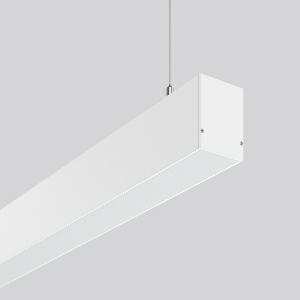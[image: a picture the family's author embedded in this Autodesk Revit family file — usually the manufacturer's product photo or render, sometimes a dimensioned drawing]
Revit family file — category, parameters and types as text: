
# Revit family: less_is_more_50_312320_002_a674
name_source: partatom
category: Lighting Fixtures
units: mm (PartAtom-declared; Revit-internal decimal feet)

## family parameters
Cut with Voids When Loaded = No
Host = Face
Light Source = No
Part Type = Normal
Room Calculation Point = No
Round Connector Dimension = Use Diameter
Shared = No

## types (1)
- LESS IS MORE 50 (1 x LED Modul 830, 6900 lm, 3000)
    Apparent Load = 59 VA
    CIE Flux Codes = 49 80 96 63 100
    Color Rendering = 80
    Color Temperature = 3000
    Default Elevation = 1800 mm
    Description = Series: LESS IS MORE 50
Linear pendant luminaire for aesthetically sophisticated lighting. Housing: extruded aluminium profile, powder-coated. End cap aluminium powder-coated. Canopy made of aluminium, powder-coated. Diffuser made of non-yellowing plastic (PMMA), opal. Direct 65%, indirect 35% light emission. Suitable for pendant. 2-point steel cable suspension freely positionable and infinitely height-adjustable. Special lengths available on request. LED unit with integrated converter interchangeable and removable. Suitable for through-wiring. With sensors or as a safety luminaire on request. 
Colour: traffic white, matt (RAL 9016)
Length: 1687 mm
Width: 57 mm
Height: 75 mm
Suspension length: 2000 mm
Lamp: LED
Socket: without socket
Colour temperature: 3000K
Colour rendering index (CRI): 80
Light source: LED
Socket lamp2: Without base
Colour temperature: 3000K
System power: 59 W
Rated luminous flux: 6900 lm
Luminous efficiency: 117 lm/W
Control gear: Regulated power supply
Control gear: Regulated power supply
Protection class: I
Type of protection: IP 20
    Height = 75 mm
    Lamp = 1 x LED Modul 830
    Lamp Light Flux = 6900 lm
    Lamp count = 1
    Length = 1687 mm
    Lifetime = 50000 h
    Luminous efficacy = 117 lm/W
    Manufacturer = RZB
    ModVariant = No
    Model = 312320.002
    Mounting Place = Ceiling
    Mounting Type = Pendant
    Number of Poles = 1
    OnlyDefault = Yes
    Power Factor = 1
    Product Name = LESS IS MORE 50
    Product group = Pendant LED linear luminaires
    ProductGroupID = 907
    Protection Class = Protection class I
    Protection Degree = IP 20
    RLX_Detail_Level = 1
    RLX_Emergency_Light_Flux = 0 lm
    RLX_Emergency_Type = 0
    RLX_Emergency_Type_DB = No
    RlxData = <blob elided: 31597 chars, md5=41d7f6b1>
    Socket = socket
    Standby Power = 0 W
    System Light Flux = 6900 lm
    System Power = 59 W
    Type Comments = Product without accessories
    Type Image = 312318.002.jpg
    URL = http://relux.com
    VarID = ---
    Voltage = 230 V
    Voltage Range = 220-240 V
    Weight = 0.00 kg
    Width = 57 mm

## geometry (parser evidence)
native form markers: Blend x4, Sweep x12
no freeform markers — native parametric forms only
